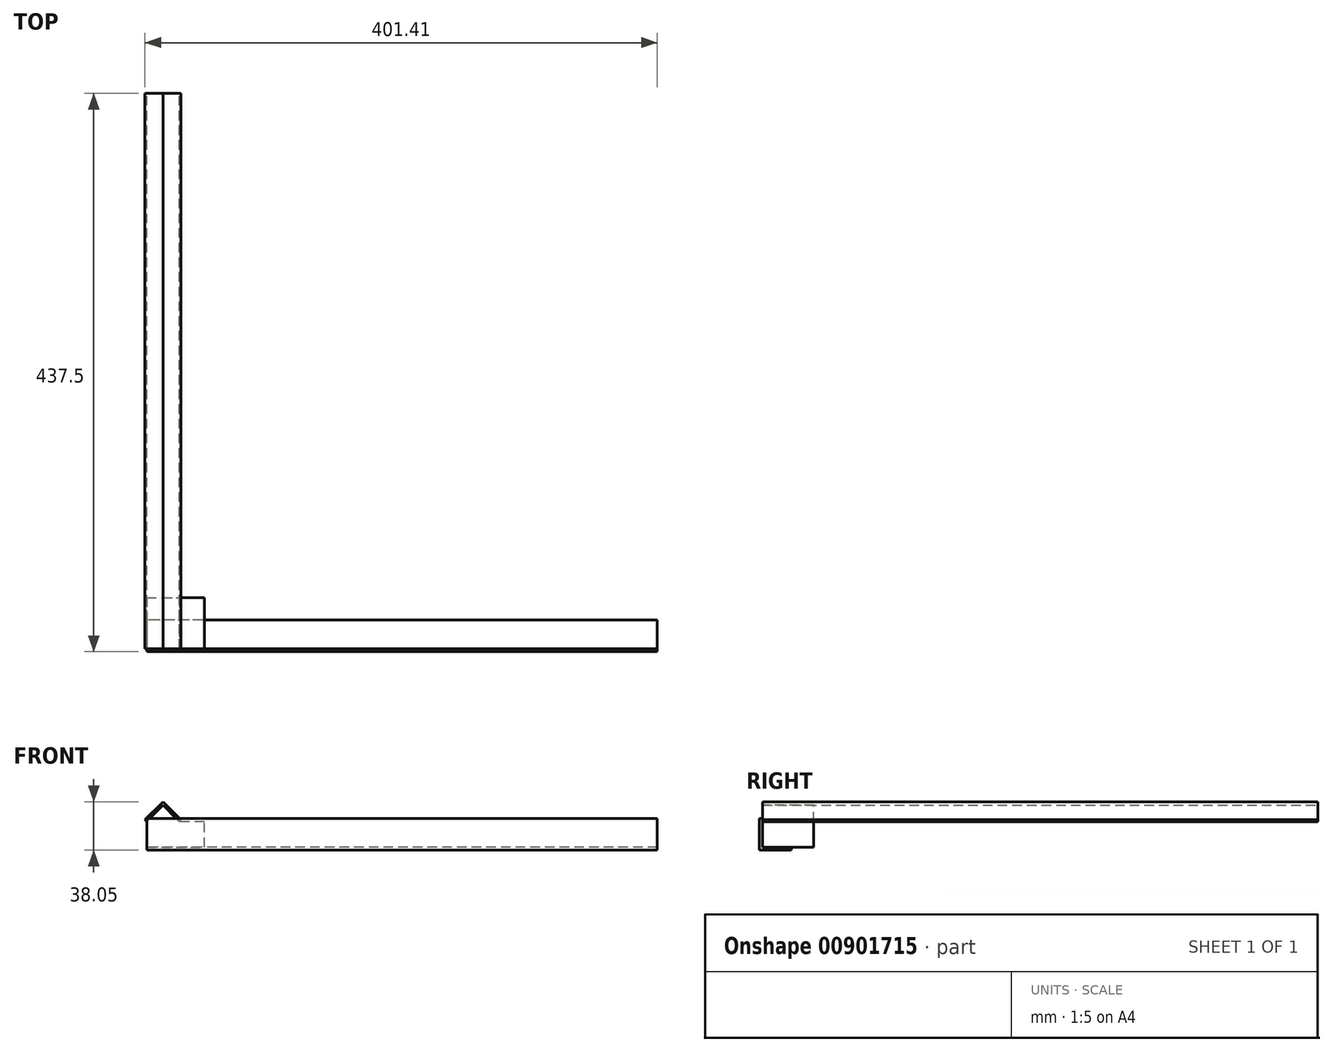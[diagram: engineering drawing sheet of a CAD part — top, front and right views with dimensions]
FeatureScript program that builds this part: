
annotation { "Feature Type Name" : "Feature", "Feature Type Description" : "" }
export const myFeature = defineFeature(function(context is Context, id is Id, definition is map)
    precondition{}
    {
        {
            var Q0;
            Q0=qCreatedBy(makeId("Front.planeOp"),FACE);
            var sketch = newSketch(context, id + "F0", { "sketchPlane" : qUnion([Q0])});
            skLineSegment(sketch, "E0", {"start": v(-173.23, 0) * mm, "end": v(-187.37, 14.14) * mm});
            skLineSegment(sketch, "E1", {"start": v(-187.37, 14.14) * mm, "end": v(-201.51, 0) * mm});
            skLineSegment(sketch, "E2", {"start": v(-201.51, 0) * mm, "end": v(-200.1, -1.41) * mm});
            skLineSegment(sketch, "E3", {"start": v(-200.1, -1.41) * mm, "end": v(-187.37, 11.31) * mm});
            skLineSegment(sketch, "E4", {"start": v(-187.37, 11.31) * mm, "end": v(-174.64, -1.41) * mm});
            skLineSegment(sketch, "E5", {"start": v(-174.64, -1.41) * mm, "end": v(-173.23, 0) * mm});
            skSolve(sketch);
        }
        {
            var Q0;
            Q0 = qSketchRegion(id + "F0", true);
            extrude(context, id + "F1", {"entities" : qUnion([Q0]), "endBound" : BoundingType.SYMMETRIC, "depth" : 410 * mm, "offsetDistance" : 25 * mm});
        }
        {
            var Q0;
            Q0=makeQuery(id+"F1.opExtrude","CAP_FACE",FACE,{"disambiguationData":[OSD([sQuery(id+"F0.wireOp",EDGE,"E0"),sQuery(id+"F0.wireOp",EDGE,"E1"),sQuery(id+"F0.wireOp",EDGE,"E2"),sQuery(id+"F0.wireOp",EDGE,"E3"),sQuery(id+"F0.wireOp",EDGE,"E4"),sQuery(id+"F0.wireOp",EDGE,"E5")])],"isStart":false});
            extrude(context, id + "F2", {"entities" : qUnion([Q0]), "operationType" : NewBodyOperationType.ADD, "depth" : 25 * mm, "offsetDistance" : 25 * mm});
        }
        {
            var Q0;
            Q0=makeQuery(id+"F2.opExtrude","CAP_FACE",FACE,{"disambiguationData":[OSD([sQuery(id+"F0.wireOp",EDGE,"E0"),sQuery(id+"F0.wireOp",EDGE,"E1"),sQuery(id+"F0.wireOp",EDGE,"E2"),sQuery(id+"F0.wireOp",EDGE,"E3"),sQuery(id+"F0.wireOp",EDGE,"E4"),sQuery(id+"F0.wireOp",EDGE,"E5")])],"isStart":false});
            var sketch = newSketch(context, id + "F3", { "sketchPlane" : qUnion([Q0])});
            skLineSegment(sketch, "E6", {"start": v(-187.37, 11.31) * mm, "end": v(-200.1, -1.41) * mm});
            skLineSegment(sketch, "E7", {"start": v(-200.1, -1.41) * mm, "end": v(-200.1, -21.41) * mm});
            skLineSegment(sketch, "E8", {"start": v(-200.1, -21.41) * mm, "end": v(-155, -21.41) * mm});
            skLineSegment(sketch, "E9", {"start": v(-155, -21.41) * mm, "end": v(-155, -1.41) * mm});
            skLineSegment(sketch, "E10", {"start": v(-155, -1.41) * mm, "end": v(-174.64, -1.41) * mm});
            skLineSegment(sketch, "E11", {"start": v(-174.64, -1.41) * mm, "end": v(-187.37, 11.31) * mm});
            skSolve(sketch);
        }
        {
            var Q0;
            Q0=makeQuery(id+"F3.imprint","IMPRINT",FACE,{"disambiguationData":[TD([[makeQuery(id+"F3.imprint","IMPRINT",EDGE,{"derivedFrom":sQuery(id+"F3.wireOp",EDGE,"E6")}),-1.0]])]});
            extrude(context, id + "F4", {"entities" : qUnion([Q0]), "oppositeDirection" : true, "depth" : 40 * mm, "offsetDistance" : 25 * mm});
        }
        {
            var Q0;
            Q0=makeQuery(id+"F4.opExtrude","SWEPT_FACE",FACE,{"disambiguationData":[OSD([sQuery(id+"F3.wireOp",EDGE,"E7")])]});
            var sketch = newSketch(context, id + "F5", { "sketchPlane" : qUnion([Q0])});
            skLineSegment(sketch, "E12", {"start": v(230, -21.41) * mm, "end": v(207.5, -21.41) * mm});
            skLineSegment(sketch, "E13", {"start": v(207.5, -21.41) * mm, "end": v(207.5, -23.91) * mm});
            skLineSegment(sketch, "E14", {"start": v(207.5, -23.91) * mm, "end": v(232.5, -23.91) * mm});
            skLineSegment(sketch, "E15", {"start": v(232.5, -23.91) * mm, "end": v(232.5, 1.09) * mm});
            skLineSegment(sketch, "E16", {"start": v(232.5, 1.09) * mm, "end": v(230, 1.09) * mm});
            skLineSegment(sketch, "E17", {"start": v(230, 1.09) * mm, "end": v(230, -21.41) * mm});
            skSolve(sketch);
        }
        {
            var Q0;
            Q0 = qSketchRegion(id + "F5", true);
            extrude(context, id + "F6", {"entities" : qUnion([Q0]), "oppositeDirection" : true, "depth" : 400 * mm, "offsetDistance" : 25 * mm});
        }
    });
